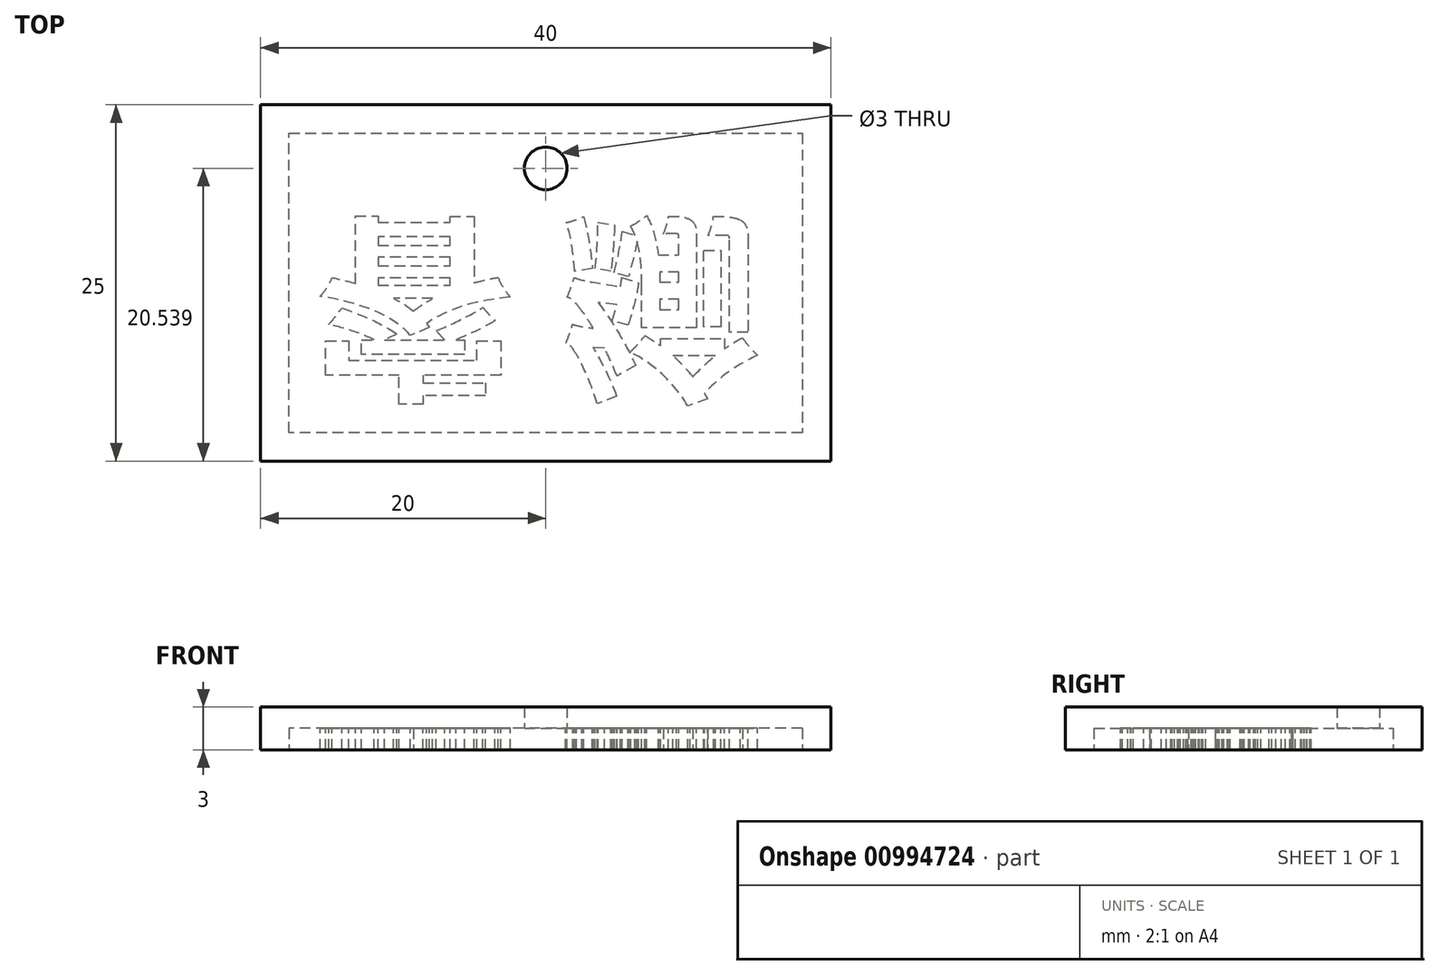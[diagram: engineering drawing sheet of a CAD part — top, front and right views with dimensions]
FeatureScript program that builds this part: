
annotation { "Feature Type Name" : "Feature", "Feature Type Description" : "" }
export const myFeature = defineFeature(function(context is Context, id is Id, definition is map)
    precondition{}
    {
        {
            var Q0;
            Q0=qCreatedBy(makeId("Top.planeOp"),FACE);
            var sketch = newSketch(context, id + "F0", { "sketchPlane" : qUnion([Q0])});
            skLineSegment(sketch, "E0.bottom", {"start": v(20, 12.5) * mm, "end": v(-20, 12.5) * mm});
            skLineSegment(sketch, "E0.top", {"start": v(20, -12.5) * mm, "end": v(-20, -12.5) * mm});
            skLineSegment(sketch, "E0.left", {"start": v(20, 12.5) * mm, "end": v(20, -12.5) * mm});
            skLineSegment(sketch, "E0.right", {"start": v(-20, 12.5) * mm, "end": v(-20, -12.5) * mm});
            skPoint(sketch, "E0.middle", {"position": v(0, 0) * mm});
            skSolve(sketch);
        }
        {
            var Q0;
            Q0 = qSketchRegion(id + "F0", true);
            extrude(context, id + "F1", {"entities" : qUnion([Q0]), "depth" : 3 * mm, "offsetDistance" : 25 * mm});
        }
        {
            var Q0;
            Q0=qCreatedBy(makeId("Top.planeOp"),FACE);
            var sketch = newSketch(context, id + "F2", { "sketchPlane" : qUnion([Q0])});
            skLineSegment(sketch, "E1.0", {"start": v(18, -10.5) * mm, "end": v(-18, -10.5) * mm});
            skLineSegment(sketch, "E1.1", {"start": v(18, 10.5) * mm, "end": v(18, -10.5) * mm});
            skLineSegment(sketch, "E1.2", {"start": v(-18, 10.5) * mm, "end": v(18, 10.5) * mm});
            skLineSegment(sketch, "E1.3", {"start": v(-18, -10.5) * mm, "end": v(-18, 10.5) * mm});
            skSolve(sketch);
        }
        {
            var Q0;
            Q0 = qSketchRegion(id + "F2", true);
            extrude(context, id + "F3", {"entities" : qUnion([Q0]), "operationType" : NewBodyOperationType.REMOVE, "depth" : 1.5 * mm, "offsetDistance" : 25 * mm});
        }
        {
            var Q0;
            Q0=makeQuery(id+"F3.boolean.opBoolean","COPY",FACE,{"derivedFrom":makeQuery(id+"F3.opExtrude","CAP_FACE",FACE,{"disambiguationData":[OSD([sQuery(id+"F2.wireOp",EDGE,"E1.0"),sQuery(id+"F2.wireOp",EDGE,"E1.1"),sQuery(id+"F2.wireOp",EDGE,"E1.2"),sQuery(id+"F2.wireOp",EDGE,"E1.3")])],"isStart":false})});
            var sketch = newSketch(context, id + "F4", { "sketchPlane" : qUnion([Q0])});
            skCircle(sketch, "E2", {"center": v(0, -8.04) * mm, "radius": 1.5 * mm});
            skSolve(sketch);
        }
        {
            var Q0;
            Q0 = qSketchRegion(id + "F4", true);
            extrude(context, id + "F5", {"entities" : qUnion([Q0]), "operationType" : NewBodyOperationType.REMOVE, "endBound" : BoundingType.THROUGH_ALL, "oppositeDirection" : true, "depth" : 1.5 * mm, "offsetDistance" : 25 * mm});
        }
        {
            var Q0;
            Q0=makeQuery(id+"F3.boolean.opBoolean","COPY",FACE,{"derivedFrom":makeQuery(id+"F3.opExtrude","CAP_FACE",FACE,{"disambiguationData":[OSD([sQuery(id+"F2.wireOp",EDGE,"E1.0"),sQuery(id+"F2.wireOp",EDGE,"E1.1"),sQuery(id+"F2.wireOp",EDGE,"E1.2"),sQuery(id+"F2.wireOp",EDGE,"E1.3")])],"isStart":false})});
            var sketch = newSketch(context, id + "F6", { "sketchPlane" : qUnion([Q0])});
            skText(sketch, "E3", { "text": "睿 緰", "fontName": "NotoSansCJKtc-Bold.otf"});
            const initialGuessF6  = {"E3": [-0.01636, -0.00351, 1, 0, 0.0102]};
            skSetInitialGuess(sketch, initialGuessF6);
            skSolve(sketch);
        }
        {
            var Q0;
            Q0 = qSketchRegion(id + "F6", true);
            extrude(context, id + "F7", {"entities" : qUnion([Q0]), "operationType" : NewBodyOperationType.ADD, "depth" : 1.5 * mm, "offsetDistance" : 25 * mm});
        }
    });
